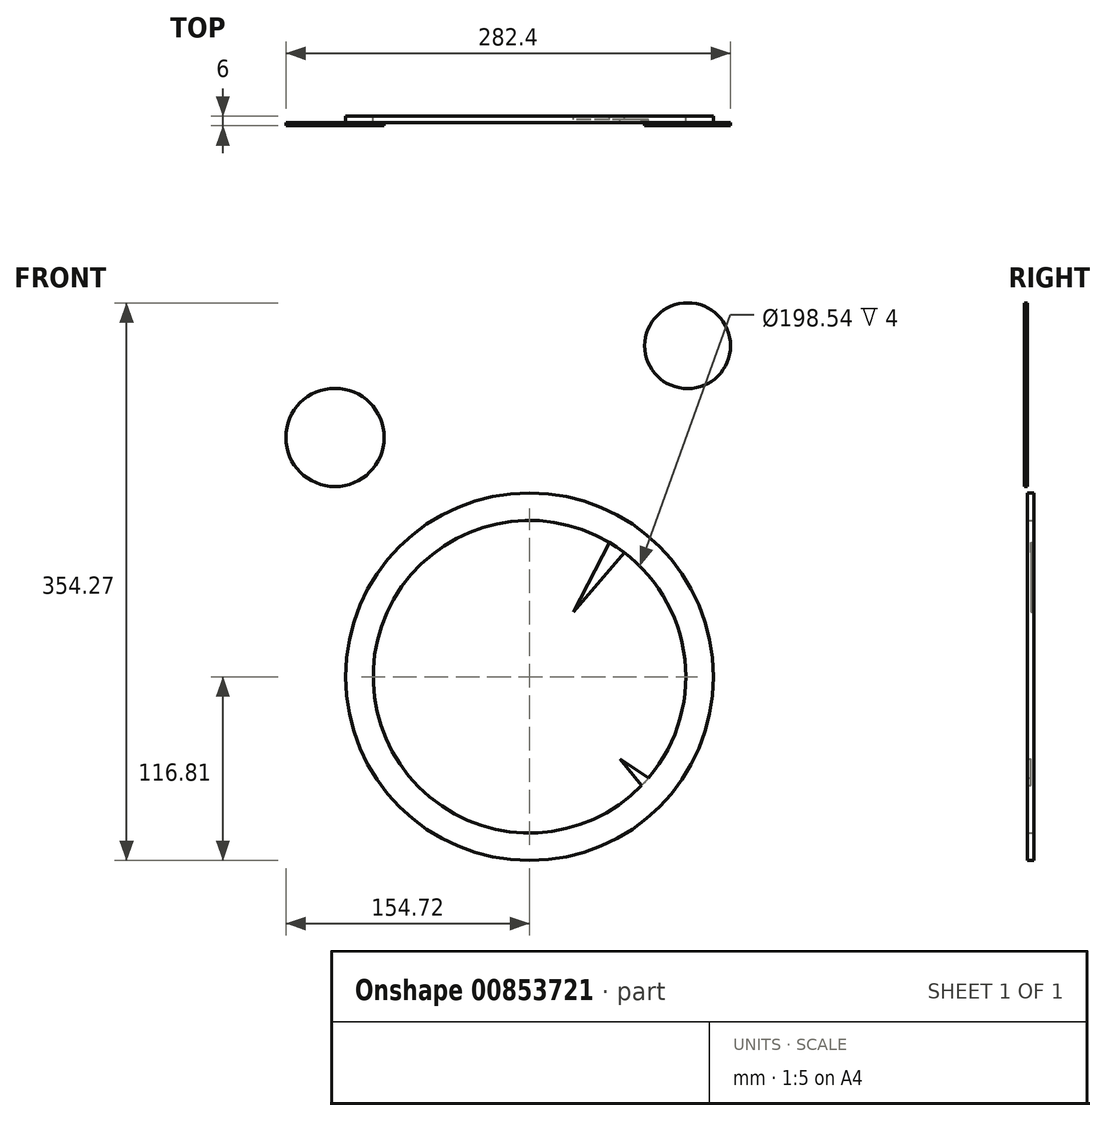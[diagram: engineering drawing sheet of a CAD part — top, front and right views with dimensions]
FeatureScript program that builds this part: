
annotation { "Feature Type Name" : "Feature", "Feature Type Description" : "" }
export const myFeature = defineFeature(function(context is Context, id is Id, definition is map)
    precondition{}
    {
        {
            var Q0;
            Q0=qCreatedBy(makeId("Front.planeOp"),FACE);
            var sketch = newSketch(context, id + "F0", { "sketchPlane" : qUnion([Q0])});
            skArc(sketch, "E0", {"start": v(50.7, 85.35) * mm, "mid": v(-55.62, -82.23) * mm, "end": v(60.35, 78.82) * mm});
            skCircle(sketch, "E1", {"center": v(0, 0) * mm, "radius": 116.8 * mm});
            skLineSegment(sketch, "E2", {"start": v(0, 0) * mm, "end": v(55.62, 82.23) * mm, "construction": true});
            skLineSegment(sketch, "E3", {"start": v(50.7, 85.35) * mm, "end": v(27.81, 41.11) * mm});
            skLineSegment(sketch, "E4.MirrorCS", {"start": v(60.35, 78.82) * mm, "end": v(27.81, 41.11) * mm});
            skSolve(sketch);
        }
        {
            var Q0;
            Q0 = qSketchRegion(id + "F0", true);
            extrude(context, id + "F1", {"entities" : qUnion([Q0]), "depth" : 2 * mm, "offsetDistance" : 25.4 * mm});
        }
        {
            var Q0;
            Q0=makeQuery(id+"F1.opExtrude","CAP_FACE",FACE,{"disambiguationData":[OSD([sQuery(id+"F0.wireOp",EDGE,"E0"),sQuery(id+"F0.wireOp",EDGE,"E1"),sQuery(id+"F0.wireOp",EDGE,"E3"),sQuery(id+"F0.wireOp",EDGE,"E4.MirrorCS")])],"isStart":false});
            var sketch = newSketch(context, id + "F2", { "sketchPlane" : qUnion([Q0])});
            skCircle(sketch, "E5", {"center": v(0, 0) * mm, "radius": 116.8 * mm});
            skArc(sketch, "E6", {"start": v(75.71, -64.2) * mm, "mid": v(-73.53, 66.7) * mm, "end": v(71.27, -69.1) * mm});
            skLineSegment(sketch, "E7", {"start": v(0, 0) * mm, "end": v(73.53, -66.7) * mm, "construction": true});
            skLineSegment(sketch, "E8", {"start": v(75.71, -64.2) * mm, "end": v(57.44, -52.1) * mm});
            skLineSegment(sketch, "E9.MirrorCS", {"start": v(71.27, -69.1) * mm, "end": v(57.44, -52.1) * mm});
            skSolve(sketch);
        }
        {
            var Q0;
            Q0 = qSketchRegion(id + "F2", true);
            extrude(context, id + "F3", {"entities" : qUnion([Q0]), "operationType" : NewBodyOperationType.ADD, "depth" : 2 * mm, "offsetDistance" : 25.4 * mm});
        }
        {
            var Q0;
            Q0=makeQuery(id+"F3.opExtrude","CAP_FACE",FACE,{"disambiguationData":[OSD([sQuery(id+"F2.wireOp",EDGE,"E5"),sQuery(id+"F2.wireOp",EDGE,"E6"),sQuery(id+"F2.wireOp",EDGE,"E8"),sQuery(id+"F2.wireOp",EDGE,"E9.MirrorCS")])],"isStart":false});
            var sketch = newSketch(context, id + "F4", { "sketchPlane" : qUnion([Q0])});
            skCircle(sketch, "E10", {"center": v(-123.5, 151.96) * mm, "radius": 31.22 * mm});
            skCircle(sketch, "E11", {"center": v(100.43, 210.21) * mm, "radius": 27.25 * mm});
            skSolve(sketch);
        }
        {
            var Q0;
            Q0=makeQuery(id+"F4.imprint","IMPRINT",FACE,{"disambiguationData":[TD([[makeQuery(id+"F4.imprint","IMPRINT",EDGE,{"derivedFrom":sQuery(id+"F4.wireOp",EDGE,"E10")}),1.0]])]});
            var Q1;
            Q1=makeQuery(id+"F4.imprint","IMPRINT",FACE,{"disambiguationData":[TD([[makeQuery(id+"F4.imprint","IMPRINT",EDGE,{"derivedFrom":sQuery(id+"F4.wireOp",EDGE,"E11")}),1.0]])]});
            var Q2;
            Q2=sQuery(id+"F4.wireOp",EDGE,"E10");
            extrude(context, id + "F5", {"entities" : qUnion([Q0, Q1]), "surfaceEntities" : qUnion([Q2]), "depth" : 2 * mm, "offsetDistance" : 25.4 * mm});
        }
        {
            var Q0;
            Q0=makeQuery(id+"F1.opExtrude","CAP_FACE",FACE,{"disambiguationData":[OSD([sQuery(id+"F0.wireOp",EDGE,"E0"),sQuery(id+"F0.wireOp",EDGE,"E1"),sQuery(id+"F0.wireOp",EDGE,"E3"),sQuery(id+"F0.wireOp",EDGE,"E4.MirrorCS")])],"isStart":false});
            var sketch = newSketch(context, id + "F6", { "sketchPlane" : qUnion([Q0])});
            skCircle(sketch, "E12", {"center": v(100.43, 210.21) * mm, "radius": 27.25 * mm});
            skCircle(sketch, "E13", {"center": v(-123.5, 151.96) * mm, "radius": 31.22 * mm});
            skCircle(sketch, "E14", {"center": v(0, 0) * mm, "radius": 116.8 * mm, "construction": true});
            skLineSegment(sketch, "E15", {"start": v(127.65, 208.82) * mm, "end": v(116.66, -5.97) * mm});
            skLineSegment(sketch, "E16", {"start": v(82.25, 230.5) * mm, "end": v(-77.94, 87) * mm});
            skLineSegment(sketch, "E17", {"start": v(-110.32, 180.26) * mm, "end": v(49.33, 105.88) * mm});
            skLineSegment(sketch, "E18", {"start": v(-153.9, 144.83) * mm, "end": v(-113.73, -26.64) * mm});
            skSolve(sketch);
        }
        {
            var Q0;
            Q0 = qSketchRegion(id + "F6", true);
            var Q1;
            Q1=sQuery(id+"F6.wireOp",EDGE,"E16");
            var Q2;
            Q2=sQuery(id+"F6.wireOp",EDGE,"E18");
            var Q3;
            Q3=sQuery(id+"F6.wireOp",EDGE,"E15");
            extrude(context, id + "F7", {"entities" : qUnion([Q0]), "bodyType" : ToolBodyType.SURFACE, "surfaceEntities" : qUnion([Q1, Q2, Q3]), "depth" : 2 * mm, "offsetDistance" : 25 * mm});
        }
        {
            var Q0;
            Q0=sQuery(id+"F6.wireOp",EDGE,"E17");
            extrude(context, id + "F8", {"bodyType" : ToolBodyType.SURFACE, "surfaceEntities" : qUnion([Q0]), "depth" : 2 * mm, "offsetDistance" : 25 * mm});
        }
    });
